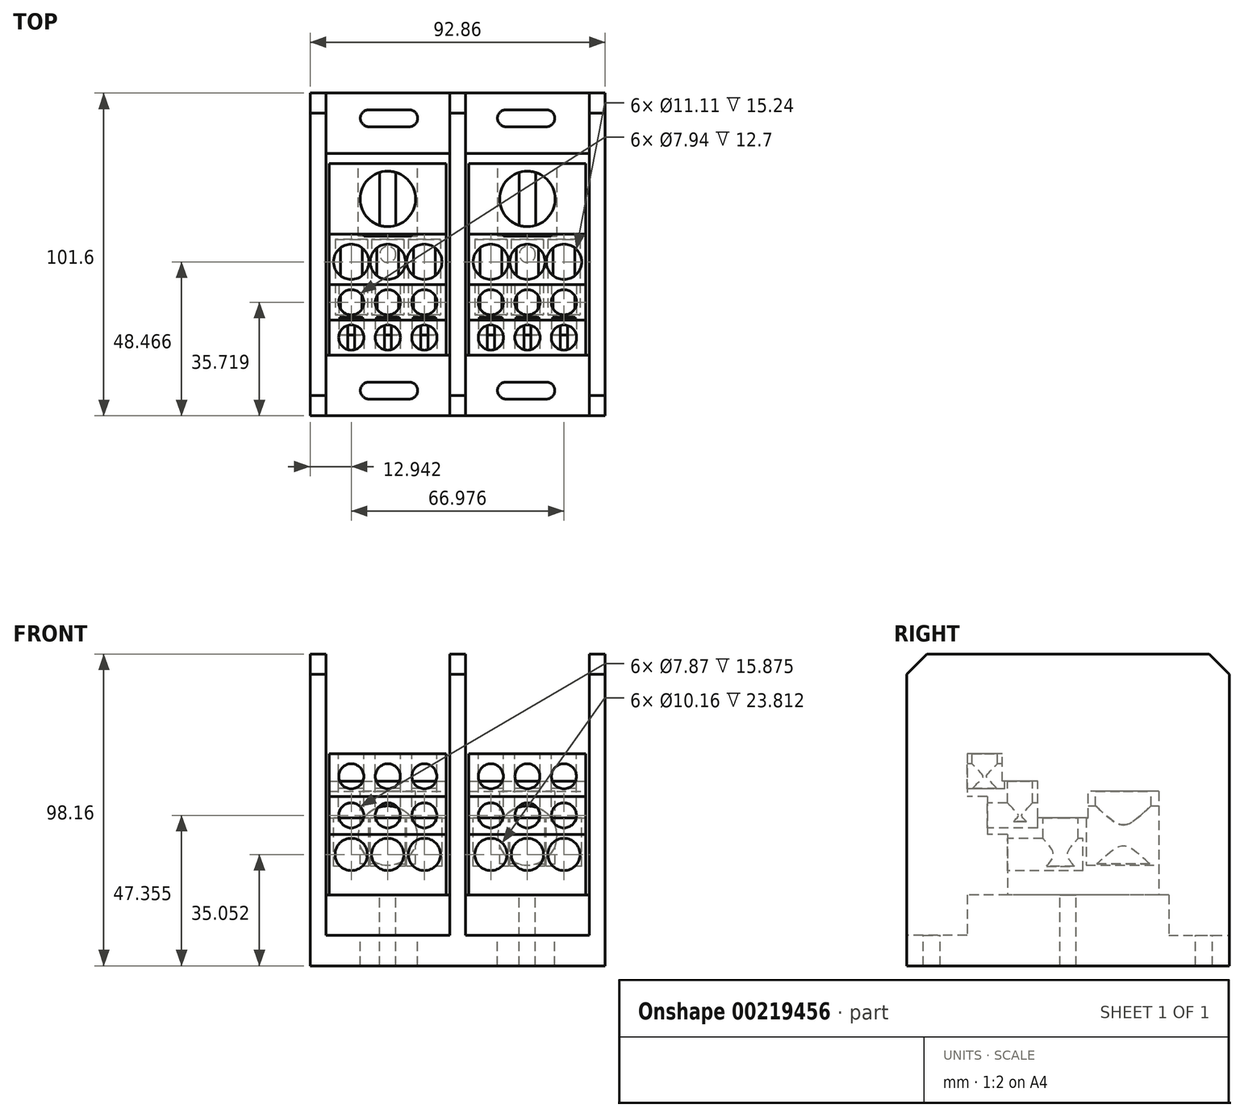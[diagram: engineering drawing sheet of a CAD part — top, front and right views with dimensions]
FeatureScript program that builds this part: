
annotation { "Feature Type Name" : "Feature", "Feature Type Description" : "" }
export const myFeature = defineFeature(function(context is Context, id is Id, definition is map)
    precondition{}
    {
        {
            var Q0;
            Q0=qCreatedBy(makeId("Top.planeOp"),FACE);
            var sketch = newSketch(context, id + "F0", { "sketchPlane" : qUnion([Q0])});
            skLineSegment(sketch, "E0.bottom", {"start": v(-46.43, -50.8) * mm, "end": v(46.43, -50.8) * mm});
            skLineSegment(sketch, "E0.top", {"start": v(-46.43, 50.8) * mm, "end": v(46.43, 50.8) * mm});
            skLineSegment(sketch, "E0.left", {"start": v(-46.43, -50.8) * mm, "end": v(-46.43, 50.8) * mm});
            skLineSegment(sketch, "E0.right", {"start": v(46.43, -50.8) * mm, "end": v(46.43, 50.8) * mm});
            skPoint(sketch, "E0.middle", {"position": v(0, 0) * mm});
            skSolve(sketch);
        }
        {
            var Q0;
            Q0=makeQuery(id+"F0.imprint","IMPRINT",FACE,{"disambiguationData":[TD([[makeQuery(id+"F0.imprint","IMPRINT",EDGE,{"derivedFrom":sQuery(id+"F0.wireOp",EDGE,"E0.bottom")}),1.0]])]});
            extrude(context, id + "F1", {"entities" : qUnion([Q0]), "depth" : 9.65 * mm});
        }
        {
            var Q0;
            Q0=makeQuery(id+"F1.opExtrude","CAP_FACE",FACE,{"disambiguationData":[OSD([sQuery(id+"F0.wireOp",EDGE,"E0.bottom"),sQuery(id+"F0.wireOp",EDGE,"E0.top"),sQuery(id+"F0.wireOp",EDGE,"E0.left"),sQuery(id+"F0.wireOp",EDGE,"E0.right")])],"isStart":false});
            var sketch = newSketch(context, id + "F2", { "sketchPlane" : qUnion([Q0])});
            skLineSegment(sketch, "E1.bottom", {"start": v(-15.24, 40.2) * mm, "end": v(-27.94, 40.2) * mm});
            skLineSegment(sketch, "E1.top", {"start": v(-15.24, 45.53) * mm, "end": v(-27.94, 45.53) * mm});
            skLineSegment(sketch, "E1.left", {"start": v(-15.24, 40.2) * mm, "end": v(-15.24, 45.53) * mm});
            skLineSegment(sketch, "E1.right", {"start": v(-27.94, 40.2) * mm, "end": v(-27.94, 45.53) * mm});
            skPoint(sketch, "E1.middle", {"position": v(-21.59, 42.86) * mm});
            skLineSegment(sketch, "E2.bottom", {"start": v(27.94, 40.2) * mm, "end": v(15.24, 40.2) * mm});
            skLineSegment(sketch, "E2.top", {"start": v(27.94, 45.53) * mm, "end": v(15.24, 45.53) * mm});
            skLineSegment(sketch, "E2.left", {"start": v(27.94, 40.2) * mm, "end": v(27.94, 45.53) * mm});
            skLineSegment(sketch, "E2.right", {"start": v(15.24, 40.2) * mm, "end": v(15.24, 45.53) * mm});
            skPoint(sketch, "E2.middle", {"position": v(21.59, 42.86) * mm});
            skPoint(sketch, "E2.middle.positionSnap0", {"position": v(-15.24, 42.86) * mm});
            skPoint(sketch, "E2.centerSnap0", {"position": v(-15.24, 42.86) * mm});
            skLineSegment(sketch, "E3.bottom", {"start": v(-15.24, -45.53) * mm, "end": v(-27.94, -45.53) * mm});
            skLineSegment(sketch, "E3.top", {"start": v(-15.24, -40.2) * mm, "end": v(-27.94, -40.2) * mm});
            skLineSegment(sketch, "E3.left", {"start": v(-15.24, -45.53) * mm, "end": v(-15.24, -40.2) * mm});
            skLineSegment(sketch, "E3.right", {"start": v(-27.94, -45.53) * mm, "end": v(-27.94, -40.2) * mm});
            skPoint(sketch, "E3.middle", {"position": v(-21.59, -42.86) * mm});
            skPoint(sketch, "E3.middle.positionSnap0", {"position": v(-21.59, 40.2) * mm});
            skPoint(sketch, "E3.centerSnap0", {"position": v(-21.59, 40.2) * mm});
            skLineSegment(sketch, "E4.bottom", {"start": v(27.94, -45.53) * mm, "end": v(15.24, -45.53) * mm});
            skLineSegment(sketch, "E4.top", {"start": v(27.94, -40.2) * mm, "end": v(15.24, -40.2) * mm});
            skLineSegment(sketch, "E4.left", {"start": v(27.94, -45.53) * mm, "end": v(27.94, -40.2) * mm});
            skLineSegment(sketch, "E4.right", {"start": v(15.24, -45.53) * mm, "end": v(15.24, -40.2) * mm});
            skPoint(sketch, "E4.middle", {"position": v(21.59, -42.86) * mm});
            skPoint(sketch, "E4.middle.positionSnap0", {"position": v(21.6, 40.2) * mm});
            skPoint(sketch, "E4.middle.positionSnap1", {"position": v(-15.24, -42.86) * mm});
            skPoint(sketch, "E4.centerSnap0", {"position": v(21.6, 40.2) * mm});
            skPoint(sketch, "E4.centerSnap1", {"position": v(-15.24, -42.86) * mm});
            skArc(sketch, "E5", {"start": v(-27.94, 45.53) * mm, "mid": v(-30.6, 42.86) * mm, "end": v(-27.94, 40.2) * mm});
            skArc(sketch, "E6", {"start": v(-15.24, 40.2) * mm, "mid": v(-12.57, 42.86) * mm, "end": v(-15.24, 45.53) * mm});
            skArc(sketch, "E7", {"start": v(15.24, 45.53) * mm, "mid": v(12.57, 42.86) * mm, "end": v(15.24, 40.2) * mm});
            skArc(sketch, "E8", {"start": v(27.94, 40.2) * mm, "mid": v(30.6, 42.86) * mm, "end": v(27.94, 45.53) * mm});
            skArc(sketch, "E9", {"start": v(-27.94, -40.2) * mm, "mid": v(-30.6, -42.86) * mm, "end": v(-27.94, -45.53) * mm});
            skArc(sketch, "E10", {"start": v(-15.24, -45.53) * mm, "mid": v(-12.57, -42.86) * mm, "end": v(-15.24, -40.2) * mm});
            skArc(sketch, "E11", {"start": v(15.24, -40.2) * mm, "mid": v(12.57, -42.86) * mm, "end": v(15.24, -45.53) * mm});
            skArc(sketch, "E12", {"start": v(27.94, -45.53) * mm, "mid": v(30.6, -42.86) * mm, "end": v(27.94, -40.2) * mm});
            skSolve(sketch);
        }
        {
            var Q0;
            Q0=qSketchRegion(id+"F2",true);
            extrude(context, id + "F3", {"entities" : qUnion([Q0]), "operationType" : NewBodyOperationType.REMOVE, "oppositeDirection" : true, "depth" : 9.65 * mm});
        }
        {
            var Q0;
            Q0=makeQuery(id+"F1.opExtrude","CAP_FACE",FACE,{"disambiguationData":[OSD([sQuery(id+"F0.wireOp",EDGE,"E0.bottom"),sQuery(id+"F0.wireOp",EDGE,"E0.top"),sQuery(id+"F0.wireOp",EDGE,"E0.left"),sQuery(id+"F0.wireOp",EDGE,"E0.right")])],"isStart":false});
            var sketch = newSketch(context, id + "F4", { "sketchPlane" : qUnion([Q0])});
            skLineSegment(sketch, "E13.bottom", {"start": v(-46.43, 50.8) * mm, "end": v(-41.48, 50.8) * mm});
            skLineSegment(sketch, "E13.top", {"start": v(-46.43, -50.8) * mm, "end": v(-41.48, -50.8) * mm});
            skLineSegment(sketch, "E13.left", {"start": v(-46.43, 50.8) * mm, "end": v(-46.43, -50.8) * mm});
            skLineSegment(sketch, "E13.right", {"start": v(-41.48, 50.8) * mm, "end": v(-41.48, -50.8) * mm});
            skLineSegment(sketch, "E14.bottom", {"start": v(46.43, 50.8) * mm, "end": v(41.48, 50.8) * mm});
            skLineSegment(sketch, "E14.top", {"start": v(46.43, -50.8) * mm, "end": v(41.48, -50.8) * mm});
            skLineSegment(sketch, "E14.left", {"start": v(46.43, 50.8) * mm, "end": v(46.43, -50.8) * mm});
            skLineSegment(sketch, "E14.right", {"start": v(41.48, 50.8) * mm, "end": v(41.48, -50.8) * mm});
            skLineSegment(sketch, "E15.bottom", {"start": v(-2.48, -50.8) * mm, "end": v(2.48, -50.8) * mm});
            skLineSegment(sketch, "E15.top", {"start": v(-2.48, 50.8) * mm, "end": v(2.48, 50.8) * mm});
            skLineSegment(sketch, "E15.left", {"start": v(-2.48, -50.8) * mm, "end": v(-2.48, 50.8) * mm});
            skLineSegment(sketch, "E15.right", {"start": v(2.48, -50.8) * mm, "end": v(2.48, 50.8) * mm});
            skPoint(sketch, "E15.middle", {"position": v(0, 0) * mm});
            skSolve(sketch);
        }
        {
            var Q0;
            Q0=qSketchRegion(id+"F4",true);
            extrude(context, id + "F5", {"entities" : qUnion([Q0]), "operationType" : NewBodyOperationType.ADD, "depth" : 88.5 * mm});
        }
        {
            var Q0;
            {var subQ0=sQuery(id+"F0.wireOp",EDGE,"E0.top");var subQ1=sQuery(id+"F0.wireOp",EDGE,"E0.bottom");Q0=makeQuery(id+"F5.boolean.opBoolean","SPLIT",FACE,{"disambiguationData":[TD([makeQuery(id+"F3.boolean.opBoolean","COPY",FACE,{"derivedFrom":makeQuery(id+"F3.opExtrude","SWEPT_FACE",FACE,{"disambiguationData":[OSD([sQuery(id+"F2.wireOp",EDGE,"E1.bottom")])]})})])],"derivedFrom":makeQuery(id+"F1.opExtrude","CAP_FACE",FACE,{"disambiguationData":[OSD([subQ1,subQ0,sQuery(id+"F0.wireOp",EDGE,"E0.left"),sQuery(id+"F0.wireOp",EDGE,"E0.right")])],"isStart":false})});}
            var sketch = newSketch(context, id + "F6", { "sketchPlane" : qUnion([Q0])});
            skLineSegment(sketch, "E16.bottom", {"start": v(-41.48, 31.75) * mm, "end": v(-2.48, 31.75) * mm});
            skLineSegment(sketch, "E16.top", {"start": v(-41.48, -31.75) * mm, "end": v(-2.48, -31.75) * mm});
            skLineSegment(sketch, "E16.left", {"start": v(-41.48, 31.75) * mm, "end": v(-41.48, -31.75) * mm});
            skLineSegment(sketch, "E16.right", {"start": v(-2.48, 31.75) * mm, "end": v(-2.48, -31.75) * mm});
            skSolve(sketch);
        }
        {
            var Q0;
            {var subQ0=sQuery(id+"F0.wireOp",EDGE,"E0.bottom");var subQ1=sQuery(id+"F0.wireOp",EDGE,"E0.top");Q0=makeQuery(id+"F5.boolean.opBoolean","SPLIT",FACE,{"disambiguationData":[TD([makeQuery(id+"F3.boolean.opBoolean","COPY",FACE,{"derivedFrom":makeQuery(id+"F3.opExtrude","SWEPT_FACE",FACE,{"disambiguationData":[OSD([sQuery(id+"F2.wireOp",EDGE,"E2.bottom")])]})})])],"derivedFrom":makeQuery(id+"F1.opExtrude","CAP_FACE",FACE,{"disambiguationData":[OSD([subQ0,subQ1,sQuery(id+"F0.wireOp",EDGE,"E0.left"),sQuery(id+"F0.wireOp",EDGE,"E0.right")])],"isStart":false})});}
            var sketch = newSketch(context, id + "F7", { "sketchPlane" : qUnion([Q0])});
            skLineSegment(sketch, "E17.bottom", {"start": v(2.48, 31.75) * mm, "end": v(41.48, 31.75) * mm});
            skLineSegment(sketch, "E17.top", {"start": v(2.48, -31.75) * mm, "end": v(41.48, -31.75) * mm});
            skLineSegment(sketch, "E17.left", {"start": v(2.48, 31.75) * mm, "end": v(2.48, -31.75) * mm});
            skLineSegment(sketch, "E17.right", {"start": v(41.48, 31.75) * mm, "end": v(41.48, -31.75) * mm});
            skSolve(sketch);
        }
        {
            var Q0;
            Q0=makeQuery(id+"F6.imprint","IMPRINT",FACE,{"disambiguationData":[TD([[makeQuery(id+"F6.imprint","IMPRINT",EDGE,{"derivedFrom":sQuery(id+"F6.wireOp",EDGE,"E16.bottom")}),-1.0]])]});
            var Q1;
            Q1=makeQuery(id+"F7.imprint","IMPRINT",FACE,{"disambiguationData":[TD([[makeQuery(id+"F7.imprint","IMPRINT",EDGE,{"derivedFrom":sQuery(id+"F7.wireOp",EDGE,"E17.bottom")}),-1.0]])]});
            extrude(context, id + "F8", {"entities" : qUnion([Q0, Q1]), "operationType" : NewBodyOperationType.ADD, "depth" : 12.7 * mm});
        }
        {
            var Q0;
            Q0=makeQuery(id+"F8.opExtrude","CAP_FACE",FACE,{"disambiguationData":[OSD([sQuery(id+"F6.wireOp",EDGE,"E16.bottom"),sQuery(id+"F6.wireOp",EDGE,"E16.top"),sQuery(id+"F6.wireOp",EDGE,"E16.left"),sQuery(id+"F6.wireOp",EDGE,"E16.right")])],"isStart":false});
            var sketch = newSketch(context, id + "F9", { "sketchPlane" : qUnion([Q0])});
            skLineSegment(sketch, "E18.bottom", {"start": v(-40.4, 28.58) * mm, "end": v(-3.56, 28.58) * mm});
            skLineSegment(sketch, "E18.top", {"start": v(-40.4, -31.75) * mm, "end": v(-3.56, -31.75) * mm});
            skLineSegment(sketch, "E18.left", {"start": v(-40.4, 28.58) * mm, "end": v(-40.4, -31.75) * mm});
            skLineSegment(sketch, "E18.right", {"start": v(-3.56, 28.58) * mm, "end": v(-3.56, -31.75) * mm});
            skSolve(sketch);
        }
        {
            var Q0;
            Q0=makeQuery(id+"F9.imprint","IMPRINT",FACE,{"disambiguationData":[TD([[makeQuery(id+"F9.imprint","IMPRINT",EDGE,{"derivedFrom":sQuery(id+"F9.wireOp",EDGE,"E18.bottom")}),-1.0]])]});
            extrude(context, id + "F10", {"entities" : qUnion([Q0]), "depth" : 44.45 * mm});
        }
        {
            var Q0;
            Q0=makeQuery(id+"F8.opExtrude","CAP_FACE",FACE,{"disambiguationData":[OSD([sQuery(id+"F6.wireOp",EDGE,"E16.bottom"),sQuery(id+"F6.wireOp",EDGE,"E16.top"),sQuery(id+"F6.wireOp",EDGE,"E16.left"),sQuery(id+"F6.wireOp",EDGE,"E16.right")])],"isStart":false});
            var sketch = newSketch(context, id + "F11", { "sketchPlane" : qUnion([Q0])});
            skCircle(sketch, "E19", {"center": v(-21.98, 0) * mm, "radius": 2.54 * mm});
            skPoint(sketch, "E19.centerSnap0", {"position": v(-21.98, 31.75) * mm});
            skPoint(sketch, "E19.centerSnap1", {"position": v(-41.48, 0) * mm});
            skSolve(sketch);
        }
        {
            var Q0;
            Q0=makeQuery(id+"F8.opExtrude","CAP_FACE",FACE,{"disambiguationData":[OSD([sQuery(id+"F7.wireOp",EDGE,"E17.bottom"),sQuery(id+"F7.wireOp",EDGE,"E17.top"),sQuery(id+"F7.wireOp",EDGE,"E17.left"),sQuery(id+"F7.wireOp",EDGE,"E17.right")])],"isStart":false});
            var sketch = newSketch(context, id + "F12", { "sketchPlane" : qUnion([Q0])});
            skCircle(sketch, "E20", {"center": v(21.98, 0) * mm, "radius": 2.54 * mm});
            skPoint(sketch, "E20.centerSnap0", {"position": v(21.98, 31.75) * mm});
            skPoint(sketch, "E20.centerSnap1", {"position": v(2.48, 0) * mm});
            skSolve(sketch);
        }
        {
            var Q0;
            Q0=makeQuery(id+"F11.imprint","IMPRINT",FACE,{"disambiguationData":[TD([[makeQuery(id+"F11.imprint","IMPRINT",EDGE,{"derivedFrom":sQuery(id+"F11.wireOp",EDGE,"E19")}),1.0]])]});
            var Q1;
            Q1=makeQuery(id+"F12.imprint","IMPRINT",FACE,{"disambiguationData":[TD([[makeQuery(id+"F12.imprint","IMPRINT",EDGE,{"derivedFrom":sQuery(id+"F12.wireOp",EDGE,"E20")}),1.0]])]});
            extrude(context, id + "F13", {"entities" : qUnion([Q0, Q1]), "operationType" : NewBodyOperationType.REMOVE, "oppositeDirection" : true, "depth" : 22.35 * mm});
        }
        {
            var Q0;
            Q0=makeQuery(id+"F10.opExtrude","CAP_FACE",FACE,{"disambiguationData":[OSD([sQuery(id+"F9.wireOp",EDGE,"E18.bottom"),sQuery(id+"F9.wireOp",EDGE,"E18.top"),sQuery(id+"F9.wireOp",EDGE,"E18.left"),sQuery(id+"F9.wireOp",EDGE,"E18.right")])],"isStart":false});
            var sketch = newSketch(context, id + "F14", { "sketchPlane" : qUnion([Q0])});
            skLineSegment(sketch, "E21.bottom", {"start": v(-40.4, 28.58) * mm, "end": v(-3.56, 28.58) * mm});
            skLineSegment(sketch, "E21.top", {"start": v(-40.4, 6.35) * mm, "end": v(-3.56, 6.35) * mm});
            skLineSegment(sketch, "E21.left", {"start": v(-40.4, 28.58) * mm, "end": v(-40.4, 6.35) * mm});
            skLineSegment(sketch, "E21.right", {"start": v(-3.56, 28.58) * mm, "end": v(-3.56, 6.35) * mm});
            skSolve(sketch);
        }
        {
            var Q0;
            Q0=makeQuery(id+"F14.imprint","IMPRINT",FACE,{"disambiguationData":[TD([[makeQuery(id+"F14.imprint","IMPRINT",EDGE,{"derivedFrom":sQuery(id+"F14.wireOp",EDGE,"E21.bottom")}),-1.0]])]});
            extrude(context, id + "F15", {"entities" : qUnion([Q0]), "operationType" : NewBodyOperationType.REMOVE, "oppositeDirection" : true, "depth" : 11.9 * mm});
        }
        {
            var Q0;
            Q0=makeQuery(id+"F10.opExtrude","CAP_FACE",FACE,{"disambiguationData":[OSD([sQuery(id+"F9.wireOp",EDGE,"E18.bottom"),sQuery(id+"F9.wireOp",EDGE,"E18.top"),sQuery(id+"F9.wireOp",EDGE,"E18.left"),sQuery(id+"F9.wireOp",EDGE,"E18.right")])],"isStart":false});
            var sketch = newSketch(context, id + "F16", { "sketchPlane" : qUnion([Q0])});
            skLineSegment(sketch, "E22.bottom", {"start": v(-40.4, 6.35) * mm, "end": v(-3.56, 6.35) * mm});
            skLineSegment(sketch, "E22.top", {"start": v(-40.4, -9.52) * mm, "end": v(-3.56, -9.52) * mm});
            skLineSegment(sketch, "E22.left", {"start": v(-40.4, 6.35) * mm, "end": v(-40.4, -9.52) * mm});
            skLineSegment(sketch, "E22.right", {"start": v(-3.56, 6.35) * mm, "end": v(-3.56, -9.52) * mm});
            skSolve(sketch);
        }
        {
            var Q0;
            Q0=makeQuery(id+"F16.imprint","IMPRINT",FACE,{"disambiguationData":[TD([[makeQuery(id+"F16.imprint","IMPRINT",EDGE,{"derivedFrom":sQuery(id+"F16.wireOp",EDGE,"E22.bottom")}),-1.0]])]});
            extrude(context, id + "F17", {"entities" : qUnion([Q0]), "operationType" : NewBodyOperationType.REMOVE, "oppositeDirection" : true, "depth" : 20.24 * mm});
        }
        {
            var Q0;
            Q0=makeQuery(id+"F10.opExtrude","CAP_FACE",FACE,{"disambiguationData":[OSD([sQuery(id+"F9.wireOp",EDGE,"E18.bottom"),sQuery(id+"F9.wireOp",EDGE,"E18.top"),sQuery(id+"F9.wireOp",EDGE,"E18.left"),sQuery(id+"F9.wireOp",EDGE,"E18.right")])],"isStart":false});
            var sketch = newSketch(context, id + "F18", { "sketchPlane" : qUnion([Q0])});
            skLineSegment(sketch, "E23.bottom", {"start": v(-40.4, -9.52) * mm, "end": v(-3.56, -9.52) * mm});
            skLineSegment(sketch, "E23.top", {"start": v(-40.4, -20.64) * mm, "end": v(-3.56, -20.64) * mm});
            skLineSegment(sketch, "E23.left", {"start": v(-40.4, -9.52) * mm, "end": v(-40.4, -20.64) * mm});
            skLineSegment(sketch, "E23.right", {"start": v(-3.56, -9.52) * mm, "end": v(-3.56, -20.64) * mm});
            skSolve(sketch);
        }
        {
            var Q0;
            Q0=makeQuery(id+"F18.imprint","IMPRINT",FACE,{"disambiguationData":[TD([[makeQuery(id+"F18.imprint","IMPRINT",EDGE,{"derivedFrom":sQuery(id+"F18.wireOp",EDGE,"E23.bottom")}),-1.0]])]});
            extrude(context, id + "F19", {"entities" : qUnion([Q0]), "operationType" : NewBodyOperationType.REMOVE, "oppositeDirection" : true, "depth" : 8.73 * mm});
        }
        {
            var Q0;
            Q0=makeQuery(id+"F10.opExtrude","SWEPT_FACE",FACE,{"disambiguationData":[OSD([sQuery(id+"F9.wireOp",EDGE,"E18.top")])]});
            var sketch = newSketch(context, id + "F20", { "sketchPlane" : qUnion([Q0])});
            skLineSegment(sketch, "E24.bottom", {"start": v(-40.4, 53.3) * mm, "end": v(-3.56, 53.3) * mm});
            skLineSegment(sketch, "E24.top", {"start": v(-40.4, 22.35) * mm, "end": v(-3.56, 22.35) * mm});
            skLineSegment(sketch, "E24.left", {"start": v(-40.4, 53.3) * mm, "end": v(-40.4, 22.35) * mm});
            skLineSegment(sketch, "E24.right", {"start": v(-3.56, 53.3) * mm, "end": v(-3.56, 22.35) * mm});
            skSolve(sketch);
        }
        {
            var Q0;
            Q0=makeQuery(id+"F20.imprint","IMPRINT",FACE,{"disambiguationData":[TD([[makeQuery(id+"F20.imprint","IMPRINT",EDGE,{"derivedFrom":sQuery(id+"F20.wireOp",EDGE,"E24.bottom")}),-1.0]])]});
            extrude(context, id + "F21", {"entities" : qUnion([Q0]), "operationType" : NewBodyOperationType.REMOVE, "oppositeDirection" : true, "depth" : 6.35 * mm});
        }
        {
            var Q0;
            Q0=makeQuery(id+"F21.boolean.opBoolean","COPY",FACE,{"derivedFrom":makeQuery(id+"F21.opExtrude","CAP_FACE",FACE,{"disambiguationData":[OSD([sQuery(id+"F20.wireOp",EDGE,"E24.bottom"),sQuery(id+"F20.wireOp",EDGE,"E24.top"),sQuery(id+"F20.wireOp",EDGE,"E24.left"),sQuery(id+"F20.wireOp",EDGE,"E24.right")])],"isStart":false})});
            var sketch = newSketch(context, id + "F22", { "sketchPlane" : qUnion([Q0])});
            skLineSegment(sketch, "E25.bottom", {"start": v(-40.4, 41.4) * mm, "end": v(-3.56, 41.4) * mm});
            skLineSegment(sketch, "E25.top", {"start": v(-40.4, 22.35) * mm, "end": v(-3.56, 22.35) * mm});
            skLineSegment(sketch, "E25.left", {"start": v(-40.4, 41.4) * mm, "end": v(-40.4, 22.35) * mm});
            skLineSegment(sketch, "E25.right", {"start": v(-3.56, 41.4) * mm, "end": v(-3.56, 22.35) * mm});
            skSolve(sketch);
        }
        {
            var Q0;
            Q0=makeQuery(id+"F22.imprint","IMPRINT",FACE,{"disambiguationData":[TD([[makeQuery(id+"F22.imprint","IMPRINT",EDGE,{"derivedFrom":sQuery(id+"F22.wireOp",EDGE,"E25.bottom")}),-1.0]])]});
            extrude(context, id + "F23", {"entities" : qUnion([Q0]), "operationType" : NewBodyOperationType.REMOVE, "oppositeDirection" : true, "depth" : 6.35 * mm});
        }
        {
            var Q0;
            Q0=makeQuery(id+"F10.opExtrude","SWEPT_FACE",FACE,{"disambiguationData":[OSD([sQuery(id+"F9.wireOp",EDGE,"E18.top")])]});
            var sketch = newSketch(context, id + "F24", { "sketchPlane" : qUnion([Q0])});
            skPoint(sketch, "E26.centerSnap0", {"position": v(-21.98, 66.8) * mm});
            skCircle(sketch, "E27", {"center": v(-21.98, 59.66) * mm, "radius": 3.94 * mm});
            skCircle(sketch, "E28", {"center": v(-10.47, 59.66) * mm, "radius": 3.94 * mm});
            skCircle(sketch, "E29", {"center": v(-33.49, 59.66) * mm, "radius": 3.94 * mm});
            skSolve(sketch);
        }
        {
            var Q0;
            Q0=qSketchRegion(id+"F24",true);
            extrude(context, id + "F25", {"entities" : qUnion([Q0]), "operationType" : NewBodyOperationType.REMOVE, "oppositeDirection" : true, "depth" : 11.9 * mm});
        }
        {
            var Q0;
            Q0=makeQuery(id+"F21.boolean.opBoolean","COPY",FACE,{"derivedFrom":makeQuery(id+"F21.opExtrude","CAP_FACE",FACE,{"disambiguationData":[OSD([sQuery(id+"F20.wireOp",EDGE,"E24.bottom"),sQuery(id+"F20.wireOp",EDGE,"E24.top"),sQuery(id+"F20.wireOp",EDGE,"E24.left"),sQuery(id+"F20.wireOp",EDGE,"E24.right")])],"isStart":false})});
            var sketch = newSketch(context, id + "F26", { "sketchPlane" : qUnion([Q0])});
            skCircle(sketch, "E30", {"center": v(-33.49, 47.36) * mm, "radius": 3.94 * mm});
            skPoint(sketch, "E30.centerSnap0", {"position": v(-40.4, 47.36) * mm});
            skCircle(sketch, "E31", {"center": v(-21.98, 47.36) * mm, "radius": 3.94 * mm});
            skPoint(sketch, "E31.centerSnap0", {"position": v(-21.98, 53.3) * mm});
            skCircle(sketch, "E32", {"center": v(-10.47, 47.36) * mm, "radius": 3.94 * mm});
            skSolve(sketch);
        }
        {
            var Q0;
            Q0=qSketchRegion(id+"F26",true);
            extrude(context, id + "F27", {"entities" : qUnion([Q0]), "operationType" : NewBodyOperationType.REMOVE, "oppositeDirection" : true, "depth" : 15.88 * mm});
        }
        {
            var Q0;
            Q0=makeQuery(id+"F23.boolean.opBoolean","COPY",FACE,{"derivedFrom":makeQuery(id+"F23.opExtrude","CAP_FACE",FACE,{"disambiguationData":[OSD([sQuery(id+"F22.wireOp",EDGE,"E25.bottom"),sQuery(id+"F22.wireOp",EDGE,"E25.top"),sQuery(id+"F22.wireOp",EDGE,"E25.left"),sQuery(id+"F22.wireOp",EDGE,"E25.right")])],"isStart":false})});
            var sketch = newSketch(context, id + "F28", { "sketchPlane" : qUnion([Q0])});
            skCircle(sketch, "E33", {"center": v(-21.98, 35.05) * mm, "radius": 5.08 * mm});
            skPoint(sketch, "E33.centerSnap0", {"position": v(-21.98, 41.4) * mm});
            skCircle(sketch, "E34", {"center": v(-10.47, 35.05) * mm, "radius": 5.08 * mm});
            skCircle(sketch, "E35", {"center": v(-33.49, 35.05) * mm, "radius": 5.08 * mm});
            skSolve(sketch);
        }
        {
            var Q0;
            Q0=qSketchRegion(id+"F28",true);
            extrude(context, id + "F29", {"entities" : qUnion([Q0]), "operationType" : NewBodyOperationType.REMOVE, "oppositeDirection" : true, "depth" : 23.8 * mm});
        }
        {
            var Q0;
            Q0=makeQuery(id+"F10.opExtrude","SWEPT_FACE",FACE,{"disambiguationData":[OSD([sQuery(id+"F9.wireOp",EDGE,"E18.bottom")])]});
            var sketch = newSketch(context, id + "F30", { "sketchPlane" : qUnion([Q0])});
            skCircle(sketch, "E36", {"center": v(21.98, 41) * mm, "radius": 9.33 * mm});
            skPoint(sketch, "E36.centerSnap0", {"position": v(21.98, 54.9) * mm});
            skSolve(sketch);
        }
        {
            var Q0;
            Q0=makeQuery(id+"F30.imprint","IMPRINT",FACE,{"disambiguationData":[TD([[makeQuery(id+"F30.imprint","IMPRINT",EDGE,{"derivedFrom":sQuery(id+"F30.wireOp",EDGE,"E36")}),1.0]])]});
            extrude(context, id + "F31", {"entities" : qUnion([Q0]), "operationType" : NewBodyOperationType.REMOVE, "oppositeDirection" : true, "depth" : 22.86 * mm});
        }
        {
            var Q0;
            Q0=makeQuery(id+"F15.boolean.opBoolean","COPY",FACE,{"derivedFrom":makeQuery(id+"F15.opExtrude","CAP_FACE",FACE,{"disambiguationData":[OSD([sQuery(id+"F14.wireOp",EDGE,"E21.bottom"),sQuery(id+"F14.wireOp",EDGE,"E21.top"),sQuery(id+"F14.wireOp",EDGE,"E21.left"),sQuery(id+"F14.wireOp",EDGE,"E21.right")])],"isStart":false})});
            var sketch = newSketch(context, id + "F32", { "sketchPlane" : qUnion([Q0])});
            skCircle(sketch, "E37", {"center": v(-21.98, 17.46) * mm, "radius": 8.73 * mm});
            skPoint(sketch, "E37.centerSnap0", {"position": v(-40.4, 17.46) * mm});
            skPoint(sketch, "E37.centerSnap1", {"position": v(-21.98, 28.58) * mm});
            skSolve(sketch);
        }
        {
            var Q0;
            Q0=makeQuery(id+"F32.imprint","IMPRINT",FACE,{"disambiguationData":[TD([[makeQuery(id+"F32.imprint","IMPRINT",EDGE,{"derivedFrom":sQuery(id+"F32.wireOp",EDGE,"E37")}),1.0]])]});
            extrude(context, id + "F33", {"entities" : qUnion([Q0]), "operationType" : NewBodyOperationType.REMOVE, "oppositeDirection" : true, "depth" : 22.86 * mm});
        }
        {
            var Q0;
            Q0=makeQuery(id+"F17.boolean.opBoolean","COPY",FACE,{"derivedFrom":makeQuery(id+"F17.opExtrude","CAP_FACE",FACE,{"disambiguationData":[OSD([sQuery(id+"F16.wireOp",EDGE,"E22.bottom"),sQuery(id+"F16.wireOp",EDGE,"E22.top"),sQuery(id+"F16.wireOp",EDGE,"E22.left"),sQuery(id+"F16.wireOp",EDGE,"E22.right")])],"isStart":false})});
            var sketch = newSketch(context, id + "F34", { "sketchPlane" : qUnion([Q0])});
            skCircle(sketch, "E38", {"center": v(-21.98, -2.33) * mm, "radius": 5.56 * mm});
            skPoint(sketch, "E38.centerSnap0", {"position": v(-21.98, -9.52) * mm});
            skCircle(sketch, "E39", {"center": v(-10.47, -2.33) * mm, "radius": 5.56 * mm});
            skCircle(sketch, "E40", {"center": v(-33.49, -2.33) * mm, "radius": 5.56 * mm});
            skSolve(sketch);
        }
        {
            var Q0;
            Q0=qSketchRegion(id+"F34",true);
            extrude(context, id + "F35", {"entities" : qUnion([Q0]), "operationType" : NewBodyOperationType.REMOVE, "oppositeDirection" : true, "depth" : 15.24 * mm});
        }
        {
            var Q0;
            Q0=makeQuery(id+"F19.boolean.opBoolean","COPY",FACE,{"derivedFrom":makeQuery(id+"F19.opExtrude","CAP_FACE",FACE,{"disambiguationData":[OSD([sQuery(id+"F18.wireOp",EDGE,"E23.bottom"),sQuery(id+"F18.wireOp",EDGE,"E23.top"),sQuery(id+"F18.wireOp",EDGE,"E23.left"),sQuery(id+"F18.wireOp",EDGE,"E23.right")])],"isStart":false})});
            var sketch = newSketch(context, id + "F36", { "sketchPlane" : qUnion([Q0])});
            skCircle(sketch, "E41", {"center": v(-21.98, -15.08) * mm, "radius": 3.97 * mm});
            skPoint(sketch, "E41.centerSnap0", {"position": v(-40.4, -15.08) * mm});
            skPoint(sketch, "E41.centerSnap1", {"position": v(-21.98, -9.52) * mm});
            skCircle(sketch, "E42", {"center": v(-10.47, -15.08) * mm, "radius": 3.97 * mm});
            skCircle(sketch, "E43", {"center": v(-33.49, -15.08) * mm, "radius": 3.97 * mm});
            skSolve(sketch);
        }
        {
            var Q0;
            Q0=qSketchRegion(id+"F36",true);
            extrude(context, id + "F37", {"entities" : qUnion([Q0]), "operationType" : NewBodyOperationType.REMOVE, "oppositeDirection" : true, "depth" : 12.7 * mm});
        }
        {
            var Q0;
            Q0=makeQuery(id+"F10.opExtrude","CAP_FACE",FACE,{"disambiguationData":[OSD([sQuery(id+"F9.wireOp",EDGE,"E18.bottom"),sQuery(id+"F9.wireOp",EDGE,"E18.top"),sQuery(id+"F9.wireOp",EDGE,"E18.left"),sQuery(id+"F9.wireOp",EDGE,"E18.right")])],"isStart":false});
            var sketch = newSketch(context, id + "F38", { "sketchPlane" : qUnion([Q0])});
            skCircle(sketch, "E44", {"center": v(-21.98, -26.2) * mm, "radius": 3.97 * mm});
            skPoint(sketch, "E44.centerSnap0", {"position": v(-21.98, -20.64) * mm});
            skPoint(sketch, "E44.centerSnap1", {"position": v(-40.4, -26.2) * mm});
            skCircle(sketch, "E45", {"center": v(-10.47, -26.2) * mm, "radius": 3.97 * mm});
            skCircle(sketch, "E46", {"center": v(-33.49, -26.2) * mm, "radius": 3.97 * mm});
            skSolve(sketch);
        }
        {
            var Q0;
            Q0=qSketchRegion(id+"F38",true);
            extrude(context, id + "F39", {"entities" : qUnion([Q0]), "operationType" : NewBodyOperationType.REMOVE, "oppositeDirection" : true, "depth" : 10.92 * mm});
        }
        {
            var Q0;
            Q0=makeQuery(id+"F10.opExtrude","SWEPT_BODY",BODY,{"disambiguationData":[OSD([sQuery(id+"F9.wireOp",EDGE,"E18.bottom"),sQuery(id+"F9.wireOp",EDGE,"E18.top"),sQuery(id+"F9.wireOp",EDGE,"E18.left"),sQuery(id+"F9.wireOp",EDGE,"E18.right")])]});
            transform(context, id + "F40", {"entities" : qUnion([Q0]), "transformType" : TransformType.TRANSLATION_3D, "dx" : 43.96 * mm, "dy" : 0 * mm, "dz" : 0 * mm, "makeCopy" : true});
        }
        {
            var Q0;
            Q0=makeQuery(id+"F5.opExtrude","CAP_EDGE",EDGE,{"disambiguationData":[OSD([sQuery(id+"F4.wireOp",EDGE,"E13.top")])],"isStart":false});
            var Q1;
            Q1=makeQuery(id+"F5.opExtrude","CAP_EDGE",EDGE,{"disambiguationData":[OSD([sQuery(id+"F4.wireOp",EDGE,"E15.bottom")])],"isStart":false});
            var Q2;
            Q2=makeQuery(id+"F5.opExtrude","CAP_EDGE",EDGE,{"disambiguationData":[OSD([sQuery(id+"F4.wireOp",EDGE,"E14.top")])],"isStart":false});
            var Q3;
            Q3=makeQuery(id+"F5.opExtrude","CAP_EDGE",EDGE,{"disambiguationData":[OSD([sQuery(id+"F4.wireOp",EDGE,"E14.bottom")])],"isStart":false});
            var Q4;
            Q4=makeQuery(id+"F5.opExtrude","CAP_EDGE",EDGE,{"disambiguationData":[OSD([sQuery(id+"F4.wireOp",EDGE,"E15.top")])],"isStart":false});
            var Q5;
            Q5=makeQuery(id+"F5.opExtrude","CAP_EDGE",EDGE,{"disambiguationData":[OSD([sQuery(id+"F4.wireOp",EDGE,"E13.bottom")])],"isStart":false});
            chamfer(context, id + "F41", {"entities" : qUnion([Q0, Q1, Q2, Q3, Q4, Q5]), "width" : 6.35 * mm, "tangentPropagation" : true});
        }
    });
